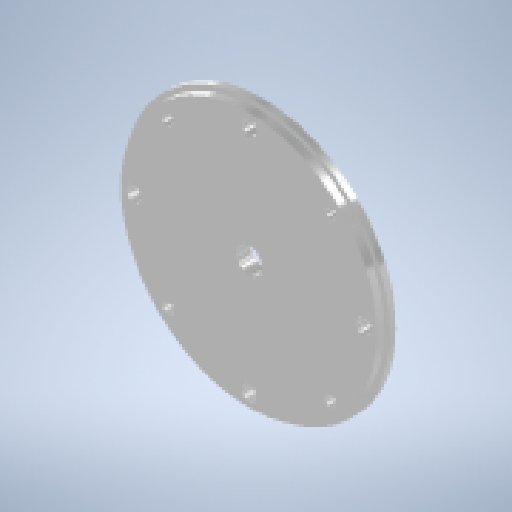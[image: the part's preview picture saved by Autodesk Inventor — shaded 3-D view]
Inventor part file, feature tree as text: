
AUTODESK INVENTOR PART (.ipt)
format: ipt  version: 2024 (Build 280153000, 153)  size: 189,952 bytes
history: native  units: mm
features: sketch x6, extrude x3, hole x3, pattern_circular x2, other x1
ambient origin geometry x8: Origin, YZ Plane, XZ Plane, XY Plane, X Axis, Y Axis, Z Axis, Center Point
bodies: Body1 (feature_tree)
feature tree (15):
  other  "ソリッド1"
  extrude  "押し出し1"  Depth=100.0mm
  extrude  "押し出し2"  Depth=2.5mm TaperAngle=0.0deg
  hole  "穴1"  [1 undecoded]
  hole  "穴2"  [1 undecoded]
  pattern_circular  "円形状パターン1"  [2 undecoded]
  hole  "穴3"  [1 undecoded]
  pattern_circular  "円形状パターン2"  Angle=45.0deg  [1 undecoded]
  extrude  "押し出し3"  Depth=40.0mm TaperAngle=360.0deg
  sketch  "スケッチ1"
  sketch  "スケッチ2"
  sketch  "スケッチ3"
  sketch  "スケッチ4"
  sketch  "スケッチ5"
  sketch  "スケッチ6"
note: 6 required parameter values undecoded (feature->parameter linkage not recoverable at this tier; creation-order binding heuristic only, values carry confidence <= 0.55)
